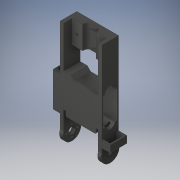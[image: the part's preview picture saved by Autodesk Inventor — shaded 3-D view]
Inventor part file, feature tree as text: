
AUTODESK INVENTOR PART (.ipt)
format: ipt  version: 2018 (Build 220112000, 112)  size: 370,176 bytes
history: native  units: in
note: dims shown in document units (in); Inventor stores cm internally (conversion verified against a paired STEP export)
features: extrude x12, sketch x10, fillet x2, imported_body x1
ambient origin geometry x8: Origin, YZ Plane, XZ Plane, XY Plane, X Axis, Y Axis, Z Axis, Center Point
bodies: Solid1 (feature_tree)
feature tree (25):
  imported_body  "Base1"
  extrude  "Extrusion1"  Depth=0.1969in TaperAngle=0.0deg
  extrude  "Extrusion2"  Depth=0.0394in
  extrude  "Extrusion3"  Depth=0.0394in TaperAngle=0.0deg
  extrude  "Extrusion4"  Depth=1.0236in
  sketch  "Sketch5"  dims[d5=0.0394in d6=2.7559in d7=0.0in]
  sketch  "Sketch7"  dims[d8=0.2362in d9=1.0236in]
  extrude  "Extrusion10"  Depth=0.3937in
  extrude  "Extrusion11"  Depth=1.0236in
  extrude  "Extrusion12"  Depth=0.3937in TaperAngle=0.0deg
  extrude  "Extrusion13"  Depth=0.0787in
  extrude  "Extrusion14"  Depth=0.0787in
  extrude  "Extrusion15"  Depth=0.0787in
  extrude  "Extrusión16"  Depth=0.0787in TaperAngle=0.0deg
  fillet  "Empalme1"  Radius=0.0787in
  extrude  "Extrusión17"  Depth=0.0787in TaperAngle=0.0deg
  fillet  "Empalme2"  Radius=0.3937in
  sketch  "Sketch3"  dims[d0=0.315in d1=0.1969in d2=0.0in]
  sketch  "Sketch4"  dims[d3=0.2756in d4=0.0394in]
  sketch  "Sketch10"  dims[d10=0.1969in d11=0.0in d12=0.3937in]
  sketch  "Sketch11"  dims[d13=0.1575in d14=0.0in d15=1.0236in]
  sketch  "Sketch12"  dims[d43=0.3937in d44=0.1969in d45=0.0in]
  sketch  "Sketch13"  dims[d50=0.0787in d51=0.0787in]
  sketch  "Boceto14"  dims[d52=0.0787in d53=0.0787in]
  sketch  "Boceto15"  dims[d54=0.1969in d55=0.0in d56=0.1181in d57=0.4724in d58=0.0in d59=0.0787in d60=0.748in d61=0.0in d62=0.3937in d63=0.0787in d64=0.0in d65=0.0787in d66=0.0in d67=0.2756in d68=0.1181in d69=0.9449in d70=0.0in d71=0.0787in d72=0.2756in d73=0.1181in d74=0.9449in d75=0.0in d76=0.0787in]
